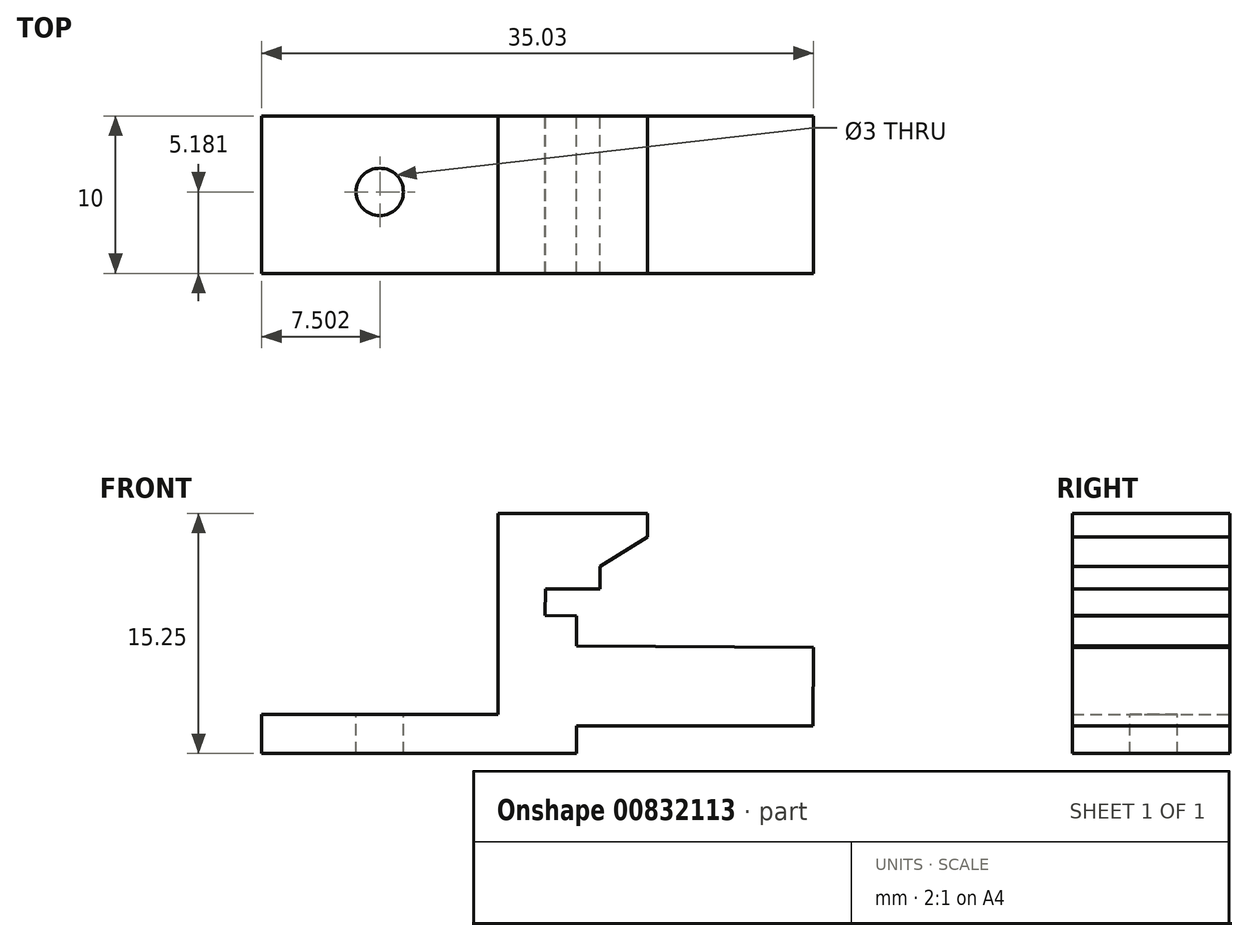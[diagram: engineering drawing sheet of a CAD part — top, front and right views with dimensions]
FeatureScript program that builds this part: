
annotation { "Feature Type Name" : "Feature", "Feature Type Description" : "" }
export const myFeature = defineFeature(function(context is Context, id is Id, definition is map)
    precondition{}
    {
        {
            var Q0;
            Q0=qCreatedBy(makeId("Front.planeOp"),FACE);
            var sketch = newSketch(context, id + "F0", { "sketchPlane" : qUnion([Q0])});
            skLineSegment(sketch, "E0.0.0", {"start": v(16.25, -0.07) * mm, "end": v(16.28, 4.93) * mm});
            skLineSegment(sketch, "E0.0.1", {"start": v(16.28, 4.93) * mm, "end": v(1.25, 5.02) * mm});
            skLineSegment(sketch, "E0.0.2", {"start": v(1.25, 5.02) * mm, "end": v(1.25, 6.93) * mm});
            skLineSegment(sketch, "E0.0.3", {"start": v(1.25, 6.93) * mm, "end": v(-0.75, 6.96) * mm});
            skLineSegment(sketch, "E0.0.4", {"start": v(-0.75, 6.96) * mm, "end": v(-0.72, 8.62) * mm});
            skLineSegment(sketch, "E0.0.5", {"start": v(-0.72, 8.62) * mm, "end": v(2.75, 8.62) * mm});
            skLineSegment(sketch, "E0.0.6", {"start": v(2.75, 8.62) * mm, "end": v(2.75, 10.05) * mm});
            skLineSegment(sketch, "E0.0.7", {"start": v(2.75, 10.05) * mm, "end": v(5.75, 11.93) * mm});
            skLineSegment(sketch, "E0.0.8", {"start": v(5.75, 11.93) * mm, "end": v(5.75, 13.43) * mm});
            skLineSegment(sketch, "E0.0.9", {"start": v(5.75, 13.43) * mm, "end": v(-3.75, 13.43) * mm});
            skLineSegment(sketch, "E0.0.10", {"start": v(-3.75, 13.43) * mm, "end": v(-3.75, 0.68) * mm});
            skLineSegment(sketch, "E0.0.18", {"start": v(1.25, -1.82) * mm, "end": v(1.25, -0.07) * mm});
            skLineSegment(sketch, "E0.0.19", {"start": v(1.25, -0.07) * mm, "end": v(16.25, -0.07) * mm});
            skPoint(sketch, "E0.0.16.end.orphan", {"position": v(-5.75, -1.82) * mm});
            skPoint(sketch, "E0.0.15.end.orphan", {"position": v(-5.75, -20.32) * mm});
            skPoint(sketch, "E0.0.13.start.orphan", {"position": v(-7.75, -22.32) * mm});
            skPoint(sketch, "E0.0.14.end.orphan", {"position": v(8.55, -20.32) * mm});
            skPoint(sketch, "E0.0.14.start.orphan", {"position": v(8.55, -22.32) * mm});
            skLineSegment(sketch, "E1.bottom", {"start": v(1.25, -1.82) * mm, "end": v(-18.75, -1.82) * mm});
            skLineSegment(sketch, "E1.top", {"start": v(-3.75, 0.68) * mm, "end": v(-18.75, 0.68) * mm});
            skLineSegment(sketch, "E1.right", {"start": v(-18.75, -1.82) * mm, "end": v(-18.75, 0.68) * mm});
            skPoint(sketch, "E0.0.11.end.orphan", {"position": v(-7.75, -0.07) * mm});
            skPoint(sketch, "E2.orphan", {"position": v(-3.75, -0.07) * mm});
            skLineSegment(sketch, "E3.0", {"start": v(4.28, 5) * mm, "end": v(4.3, 8.5) * mm, "construction": true});
            skSolve(sketch);
        }
        {
            var Q0;
            Q0=makeQuery(id+"F0.imprint","IMPRINT",FACE,{"disambiguationData":[TD([[makeQuery(id+"F0.imprint","IMPRINT",EDGE,{"derivedFrom":sQuery(id+"F0.wireOp",EDGE,"E0.0.0")}),1.0]])]});
            extrude(context, id + "F1", {"entities" : qUnion([Q0]), "depth" : 10 * mm, "offsetDistance" : 25 * mm});
        }
        {
            var Q0;
            Q0=makeQuery(id+"F1.opExtrude","SWEPT_FACE",FACE,{"disambiguationData":[OSD([sQuery(id+"F0.wireOp",EDGE,"E1.top")])]});
            var sketch = newSketch(context, id + "F2", { "sketchPlane" : qUnion([Q0])});
            skCircle(sketch, "E4", {"center": v(-11.25, -4.82) * mm, "radius": 1.5 * mm});
            skPoint(sketch, "E4.centerSnap0", {"position": v(-11.25, 0) * mm});
            skSolve(sketch);
        }
        {
            var Q0;
            Q0 = qSketchRegion(id + "F2", true);
            extrude(context, id + "F3", {"entities" : qUnion([Q0]), "operationType" : NewBodyOperationType.REMOVE, "oppositeDirection" : true, "depth" : 25 * mm, "offsetDistance" : 25 * mm});
        }
    });
